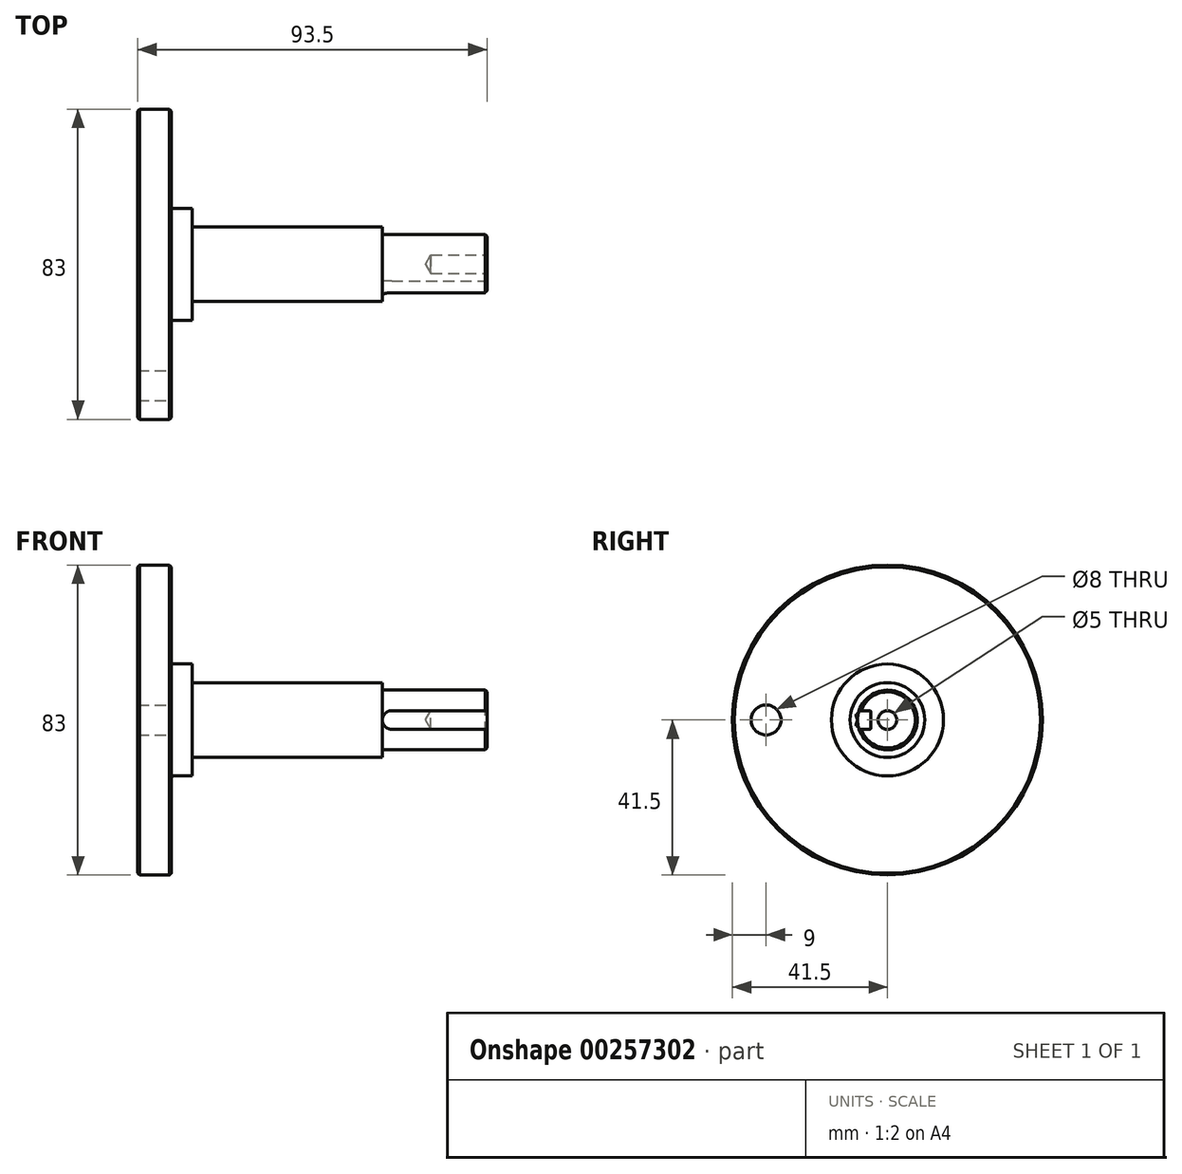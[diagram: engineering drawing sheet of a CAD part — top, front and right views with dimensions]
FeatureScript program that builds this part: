
annotation { "Feature Type Name" : "Feature", "Feature Type Description" : "" }
export const myFeature = defineFeature(function(context is Context, id is Id, definition is map)
    precondition{}
    {
        {
            var Q0;
            Q0=qCreatedBy(makeId("Front.planeOp"),FACE);
            var sketch = newSketch(context, id + "F0", { "sketchPlane" : qUnion([Q0])});
            skLineSegment(sketch, "E0", {"start": v(0, 0) * mm, "end": v(0, 41.5) * mm});
            skLineSegment(sketch, "E1", {"start": v(0, 41.5) * mm, "end": v(9, 41.5) * mm});
            skLineSegment(sketch, "E2", {"start": v(9, 41.5) * mm, "end": v(9, 15) * mm});
            skLineSegment(sketch, "E3", {"start": v(9, 15) * mm, "end": v(14.5, 15) * mm});
            skLineSegment(sketch, "E4", {"start": v(14.5, 15) * mm, "end": v(14.5, 10) * mm});
            skLineSegment(sketch, "E5", {"start": v(14.5, 10) * mm, "end": v(65.5, 10) * mm});
            skLineSegment(sketch, "E6", {"start": v(65.5, 10) * mm, "end": v(65.5, 8) * mm});
            skLineSegment(sketch, "E7", {"start": v(65.5, 8) * mm, "end": v(93.5, 8) * mm});
            skLineSegment(sketch, "E8", {"start": v(93.5, 8) * mm, "end": v(93.5, 0) * mm});
            skLineSegment(sketch, "E9", {"start": v(93.5, 0) * mm, "end": v(0, 0) * mm});
            skLineSegment(sketch, "E10", {"start": v(-13.74, 0) * mm, "end": v(100.51, 0) * mm, "construction": true});
            skSolve(sketch);
        }
        {
            var Q0;
            Q0=makeQuery(id+"F0.imprint","IMPRINT",FACE,{"disambiguationData":[TD([[makeQuery(id+"F0.imprint","IMPRINT",EDGE,{"derivedFrom":sQuery(id+"F0.wireOp",EDGE,"E0")}),-1.0]])]});
            var Q1;
            Q1=sQuery(id+"F0.wireOp",EDGE,"E10");
            revolve(context, id + "F1", {"entities" : qUnion([Q0]), "axis" : qUnion([Q1]), "revolveType" : RevolveType.FULL});
        }
        {
            var Q0;
            Q0=makeQuery(id+"F1.opRevolve","SWEPT_FACE",FACE,{"disambiguationData":[OSD([sQuery(id+"F0.wireOp",EDGE,"E2")])]});
            var sketch = newSketch(context, id + "F2", { "sketchPlane" : qUnion([Q0])});
            skPoint(sketch, "E11", {"position": v(-32.5, 0) * mm});
            skSolve(sketch);
        }
        {
            var Q0;
            Q0=sQuery(id+"F2.wireOp",VERTEX,"E11");
            var Q1;
            Q1=makeQuery(id+"F1.opRevolve","SWEPT_BODY",BODY,{"disambiguationData":[OSD([sQuery(id+"F0.wireOp",EDGE,"E0"),sQuery(id+"F0.wireOp",EDGE,"E1"),sQuery(id+"F0.wireOp",EDGE,"E2"),sQuery(id+"F0.wireOp",EDGE,"E3"),sQuery(id+"F0.wireOp",EDGE,"E4"),sQuery(id+"F0.wireOp",EDGE,"E5"),sQuery(id+"F0.wireOp",EDGE,"E6"),sQuery(id+"F0.wireOp",EDGE,"E7"),sQuery(id+"F0.wireOp",EDGE,"E8"),sQuery(id+"F0.wireOp",EDGE,"E9")])]});
            hole(context, id + "F3", {"style" : HoleStyle.SIMPLE, "endStyle" : HoleEndStyle.THROUGH, "holeDiameter" : 8 * mm, "tappedDepth" : 12 * mm, "tapClearance" : 3, "locations" : qUnion([Q0]), "scope" : qUnion([Q1])});
        }
        {
            var Q0;
            Q0=makeQuery(id+"F1.opRevolve","SWEPT_FACE",FACE,{"disambiguationData":[OSD([sQuery(id+"F0.wireOp",EDGE,"E8")])]});
            var sketch = newSketch(context, id + "F4", { "sketchPlane" : qUnion([Q0])});
            skPoint(sketch, "E12", {"position": v(0, 0) * mm});
            skSolve(sketch);
        }
        {
            var Q0;
            Q0=sQuery(id+"F4.wireOp",VERTEX,"E12");
            var Q1;
            Q1=makeQuery(id+"F1.opRevolve","SWEPT_BODY",BODY,{"disambiguationData":[OSD([sQuery(id+"F0.wireOp",EDGE,"E0"),sQuery(id+"F0.wireOp",EDGE,"E1"),sQuery(id+"F0.wireOp",EDGE,"E2"),sQuery(id+"F0.wireOp",EDGE,"E3"),sQuery(id+"F0.wireOp",EDGE,"E4"),sQuery(id+"F0.wireOp",EDGE,"E5"),sQuery(id+"F0.wireOp",EDGE,"E6"),sQuery(id+"F0.wireOp",EDGE,"E7"),sQuery(id+"F0.wireOp",EDGE,"E8"),sQuery(id+"F0.wireOp",EDGE,"E9")])]});
            hole(context, id + "F5", {"style" : HoleStyle.SIMPLE, "endStyle" : HoleEndStyle.BLIND, "standardTappedOrClearance" : lookupTablePath({ "standard" : "ISO", "fit" : "Normal", "engagement" : "75%", "pitch" : "1 mm", "size" : "M6", "type" : "Tapped" }), "standardBlindInLast" : lookupTablePath({ "fit" : "Standard", "standard" : "ISO", "engagement" : "75%", "pitch" : "1 mm", "size" : "M6", "type" : "Tapped" }), "holeDiameter" : 5 * mm, "showTappedDepth" : true, "holeDepth" : 15 * mm, "tappedDepth" : 12 * mm, "tapClearance" : 3, "locations" : qUnion([Q0]), "scope" : qUnion([Q1]), "majorDiameter" : 6 * mm});
        }
        {
            var Q0;
            Q0=qCreatedBy(makeId("Front.planeOp"),FACE);
            cPlane(context, id + "F6", {"entities" : qUnion([Q0]), "cplaneType" : CPlaneType.OFFSET, "offset" : 8 * mm, "width" : 150 * mm, "height" : 150 * mm});
        }
        {
            var Q0;
            Q0=qCreatedBy(id+"F6.planeOp",FACE);
            var sketch = newSketch(context, id + "F7", { "sketchPlane" : qUnion([Q0])});
            skLineSegment(sketch, "E13", {"start": v(68, 2.5) * mm, "end": v(95.5, 2.5) * mm});
            skLineSegment(sketch, "E14", {"start": v(68, -2.5) * mm, "end": v(95.5, -2.5) * mm});
            skLineSegment(sketch, "E15.0", {"start": v(65.5, -10) * mm, "end": v(65.5, 10) * mm, "construction": true});
            skArc(sketch, "E16", {"start": v(68, 2.5) * mm, "mid": v(65.5, 0) * mm, "end": v(68, -2.5) * mm});
            skLineSegment(sketch, "E17", {"start": v(95.5, 2.5) * mm, "end": v(95.5, -2.5) * mm});
            skSolve(sketch);
        }
        {
            var Q0;
            Q0 = qSketchRegion(id + "F7", true);
            extrude(context, id + "F8", {"entities" : qUnion([Q0]), "operationType" : NewBodyOperationType.REMOVE, "oppositeDirection" : true, "depth" : 3.5 * mm});
        }
        {
            var Q0;
            Q0=makeQuery(id+"F1.opRevolve","SWEPT_EDGE",EDGE,{"disambiguationData":[OSD([sQuery(id+"F0.wireOp",EDGE,"E1"),sQuery(id+"F0.wireOp",EDGE,"E2")])]});
            var Q1;
            Q1=makeQuery(id+"F1.opRevolve","SWEPT_EDGE",EDGE,{"disambiguationData":[OSD([sQuery(id+"F0.wireOp",EDGE,"E0"),sQuery(id+"F0.wireOp",EDGE,"E1")])]});
            chamfer(context, id + "F9", {"entities" : qUnion([Q0, Q1]), "width" : 0.5 * mm, "tangentPropagation" : true});
        }
        {
            var Q0;
            Q0=makeQuery(id+"F1.opRevolve","SWEPT_EDGE",EDGE,{"disambiguationData":[OSD([sQuery(id+"F0.wireOp",EDGE,"E2"),sQuery(id+"F0.wireOp",EDGE,"E3")])]});
            var Q1;
            Q1=makeQuery(id+"F1.opRevolve","SWEPT_EDGE",EDGE,{"disambiguationData":[OSD([sQuery(id+"F0.wireOp",EDGE,"E4"),sQuery(id+"F0.wireOp",EDGE,"E5")])]});
            var Q2;
            Q2=makeQuery(id+"F1.opRevolve","SWEPT_EDGE",EDGE,{"disambiguationData":[OSD([sQuery(id+"F0.wireOp",EDGE,"E6"),sQuery(id+"F0.wireOp",EDGE,"E7")])]});
            fillet(context, id + "F10", {"entities" : qUnion([Q0, Q1, Q2]), "radius" : 0.5 * mm, "tangentPropagation" : true, "allowEdgeOverflow" : false});
        }
        {
            var Q0;
            Q0=makeQuery(id+"F1.opRevolve","SWEPT_EDGE",EDGE,{"disambiguationData":[OSD([sQuery(id+"F0.wireOp",EDGE,"E7"),sQuery(id+"F0.wireOp",EDGE,"E8")])]});
            chamfer(context, id + "F11", {"entities" : qUnion([Q0]), "width" : 0.5 * mm, "tangentPropagation" : true});
        }
        {
            var Q0;
            Q0=makeQuery(id+"F8.boolean.opBoolean","COPY",EDGE,{"derivedFrom":makeQuery(id+"F8.opExtrude","CAP_EDGE",EDGE,{"disambiguationData":[OSD([sQuery(id+"F7.wireOp",EDGE,"E13")])],"isStart":false})});
            fillet(context, id + "F12", {"entities" : qUnion([Q0]), "radius" : 0.2 * mm, "tangentPropagation" : true, "allowEdgeOverflow" : false});
        }
    });
